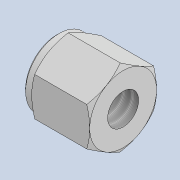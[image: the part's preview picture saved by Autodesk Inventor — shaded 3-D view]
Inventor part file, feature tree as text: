
AUTODESK INVENTOR PART (.ipt)
format: ipt  version: 2022.5 (Build 265521000, 521)  size: 170,496 bytes
history: native  units: in
note: dims shown in document units (in); Inventor stores cm internally (conversion verified against a paired STEP export)
features: sketch x4, hole x3, extrude x2, chamfer x2, revolve x1, plane x1, mirror x1
ambient origin geometry x8: Origin, YZ Plane, XZ Plane, XY Plane, X Axis, Y Axis, Z Axis, Center Point
bodies: Solid1 (feature_tree)
feature tree (14):
  sketch  "Sketch1: Hex"  dims[d1=0.0685in d2=0.2713in]
  extrude  "Ex: Hex"  Depth=0.2713in
  hole  "Hole: Tap"  [1 undecoded]
  hole  "Hole: Thread"  [1 undecoded]
  sketch  "Sketch2: Top"  dims[d47=0.145in d3=0.38in d8=0.375in d9=0.25in d10=0.5635in d11=0.23in d12=0.0in d4=0.3125in]
  extrude  "Ex: Top"  Depth=0.125in TaperAngle=45.0deg
  hole  "Hole: Tubing"  [1 undecoded]
  chamfer  "Chamfer1: Top (side)"  Distance=0.125in Angle=60.0deg
  chamfer  "Chamfer2: Top (hole)"  Distance=0.5in
  sketch  "Sketch3: Reference: Nut Chamfer"  dims[d6=0.0387in]
  sketch  "Sketch4: Chamfer (nut)"  dims[d17=0.75in d18=0.375in d19=0.25in d20=0.5635in d21=0.23in d22=0.0in d5=0.2925in d30=0.125in d31=45.0deg d43=90.0deg d45=0.125in d46=60.0deg d48=0.196in d49=0.75in d50=0.375in d51=0.25in d52=0.5635in d53=0.23in d54=0.0in d14=0.5in d15=0.0344in d16=0.5in d44=0.5in d55=1.0in d56=1.0in d57=1.0in d58=0.15in d59=0.25in d60=0.375in d61=0.5635in d62=0.75in d63=0.8108in d64=0.0625in d65=0.75in d66=0.375in]
  revolve  "Revolution: Chamfer (nut)"  [1 undecoded]
  plane  "Work Plane2: Hex Center"
  mirror  "Mirror: Chamfer (nut)"
note: 4 required parameter values undecoded (feature->parameter linkage not recoverable at this tier; creation-order binding heuristic only, values carry confidence <= 0.55)